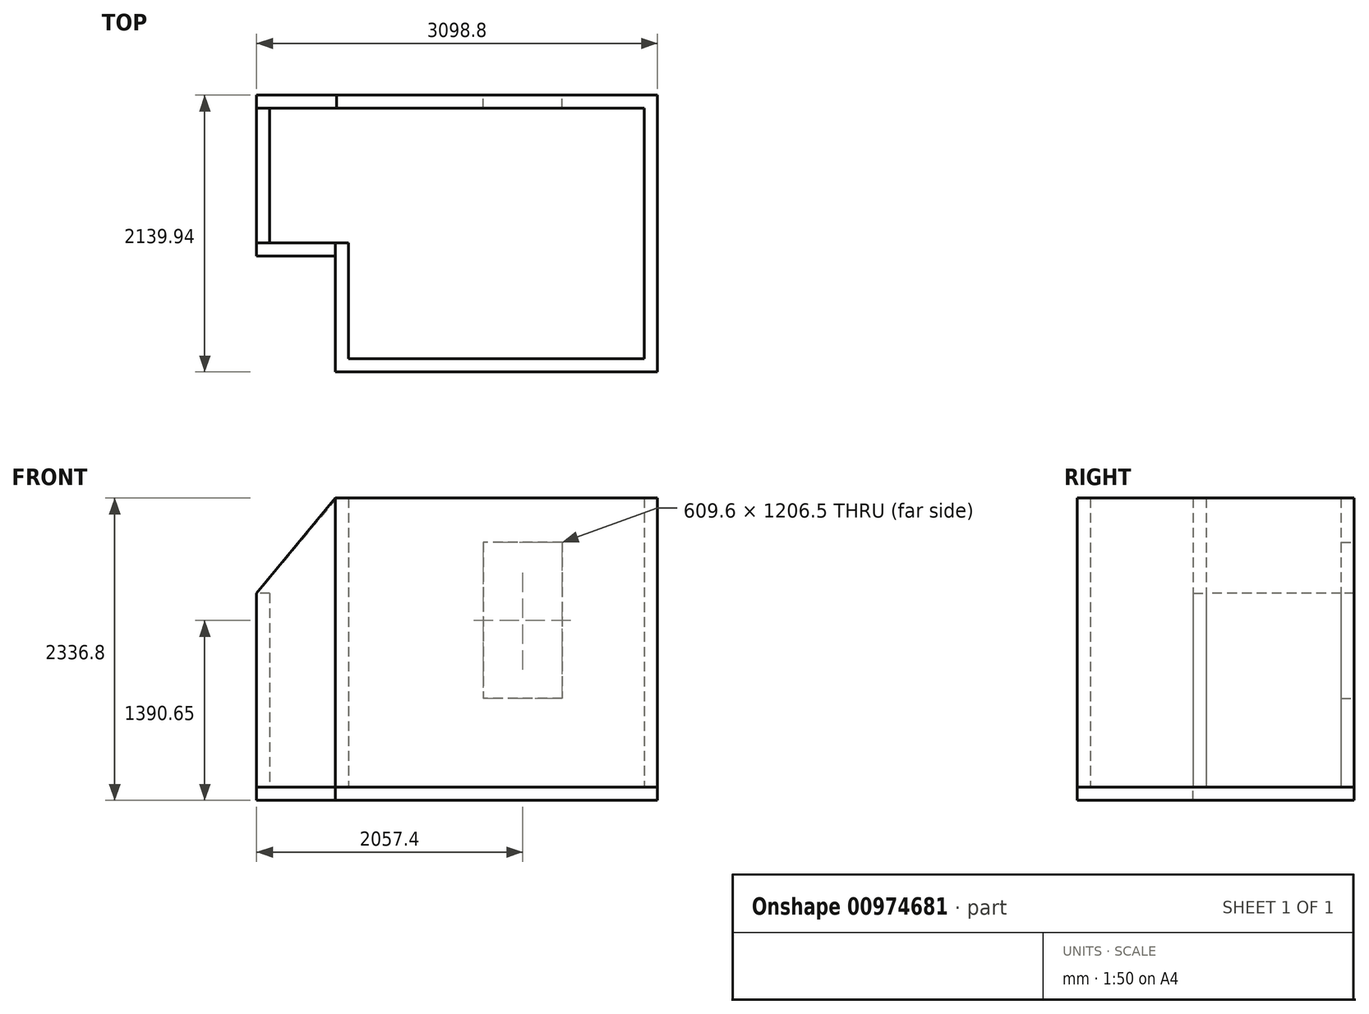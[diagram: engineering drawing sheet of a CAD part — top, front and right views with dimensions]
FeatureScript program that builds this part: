
annotation { "Feature Type Name" : "Feature", "Feature Type Description" : "" }
export const myFeature = defineFeature(function(context is Context, id is Id, definition is map)
    precondition{}
    {
        {
            var Q0;
            Q0=qCreatedBy(makeId("Top.planeOp"),FACE);
            var sketch = newSketch(context, id + "F0", { "sketchPlane" : qUnion([Q0])});
            skLineSegment(sketch, "E0.bottom", {"start": v(1143, -968.38) * mm, "end": v(-1143, -968.38) * mm});
            skLineSegment(sketch, "E0.top", {"start": v(1143, 968.38) * mm, "end": v(-1143, 968.38) * mm});
            skLineSegment(sketch, "E0.left", {"start": v(1143, -968.38) * mm, "end": v(1143, 968.38) * mm});
            skPoint(sketch, "E0.middle", {"position": v(0, 0) * mm});
            skLineSegment(sketch, "E1.bottom", {"start": v(-1143, 968.38) * mm, "end": v(-1752.6, 968.38) * mm});
            skLineSegment(sketch, "E1.top", {"start": v(-1143, -73.03) * mm, "end": v(-1752.6, -73.03) * mm});
            skLineSegment(sketch, "E1.left", {"start": v(-1143, 968.38) * mm, "end": v(-1143, -73.03) * mm});
            skLineSegment(sketch, "E1.right", {"start": v(-1752.6, 968.37) * mm, "end": v(-1752.6, -73.03) * mm});
            skPoint(sketch, "E2", {"position": v(-1143, -73.03) * mm});
            skLineSegment(sketch, "E3", {"start": v(-1143, -73.03) * mm, "end": v(-1143, -968.38) * mm});
            skLineSegment(sketch, "E4.0", {"start": v(-1244.6, -174.63) * mm, "end": v(-1244.6, -1069.98) * mm});
            skLineSegment(sketch, "E4.1", {"start": v(1244.6, -1069.97) * mm, "end": v(-1244.6, -1069.98) * mm});
            skLineSegment(sketch, "E4.2", {"start": v(-1854.2, 1069.97) * mm, "end": v(-1854.2, -174.63) * mm});
            skLineSegment(sketch, "E4.3", {"start": v(-1143, 1069.97) * mm, "end": v(-1854.2, 1069.97) * mm});
            skLineSegment(sketch, "E4.4", {"start": v(1244.6, 1069.98) * mm, "end": v(-1143, 1069.97) * mm});
            skLineSegment(sketch, "E4.5", {"start": v(-1244.6, -174.63) * mm, "end": v(-1854.2, -174.63) * mm});
            skLineSegment(sketch, "E4.6", {"start": v(1244.6, -1069.97) * mm, "end": v(1244.6, 1069.98) * mm});
            skSolve(sketch);
        }
        {
            var Q0;
            Q0=makeQuery(id+"F0.imprint","IMPRINT",FACE,{"disambiguationData":[TD([[makeQuery(id+"F0.imprint","IMPRINT",EDGE,{"derivedFrom":sQuery(id+"F0.wireOp",EDGE,"E0.bottom")}),1.0]])]});
            extrude(context, id + "F1", {"entities" : qUnion([Q0]), "depth" : 1498.6 * mm, "offsetDistance" : 25.4 * mm});
        }
        {
            var Q0;
            Q0=makeQuery(id+"F1.opExtrude","SWEPT_FACE",FACE,{"disambiguationData":[OSD([sQuery(id+"F0.wireOp",EDGE,"E4.3"),sQuery(id+"F0.wireOp",EDGE,"E4.4")])]});
            var sketch = newSketch(context, id + "F2", { "sketchPlane" : qUnion([Q0])});
            skLineSegment(sketch, "E5", {"start": v(-1244.6, 1498.6) * mm, "end": v(-1244.6, 2235.2) * mm});
            skLineSegment(sketch, "E6", {"start": v(-1244.6, 2235.2) * mm, "end": v(1236.12, 2235.2) * mm});
            skLineSegment(sketch, "E7", {"start": v(1236.12, 2235.2) * mm, "end": v(1854.2, 1498.6) * mm});
            skLineSegment(sketch, "E8", {"start": v(1854.2, 1498.6) * mm, "end": v(1854.2, 0) * mm});
            skLineSegment(sketch, "E9", {"start": v(1854.2, 0) * mm, "end": v(-1244.6, 0) * mm});
            skLineSegment(sketch, "E10", {"start": v(-1244.6, 0) * mm, "end": v(-1244.6, 1498.6) * mm});
            skLineSegment(sketch, "E11", {"start": v(1854.2, 1498.6) * mm, "end": v(-1244.6, 1498.6) * mm});
            skSolve(sketch);
        }
        {
            var Q0;
            Q0 = qSketchRegion(id + "F2", true);
            var Q1;
            Q1=makeQuery(id+"F2.imprint","IMPRINT",FACE,{"disambiguationData":[TD([[makeQuery(id+"F2.imprint","IMPRINT",EDGE,{"derivedFrom":sQuery(id+"F2.wireOp",EDGE,"E5")}),-1.0]])]});
            extrude(context, id + "F3", {"entities" : qUnion([Q0, Q1]), "operationType" : NewBodyOperationType.ADD, "oppositeDirection" : true, "depth" : 101.6 * mm, "offsetDistance" : 25.4 * mm});
        }
        {
            var Q0;
            Q0=makeQuery(id+"F1.opExtrude","CAP_FACE",FACE,{"disambiguationData":[OSD([sQuery(id+"F0.wireOp",EDGE,"E0.bottom"),sQuery(id+"F0.wireOp",EDGE,"E0.top"),sQuery(id+"F0.wireOp",EDGE,"E0.left"),sQuery(id+"F0.wireOp",EDGE,"E1.bottom"),sQuery(id+"F0.wireOp",EDGE,"E1.top"),sQuery(id+"F0.wireOp",EDGE,"E1.right"),sQuery(id+"F0.wireOp",EDGE,"E3"),sQuery(id+"F0.wireOp",EDGE,"E4.0"),sQuery(id+"F0.wireOp",EDGE,"E4.1"),sQuery(id+"F0.wireOp",EDGE,"E4.2"),sQuery(id+"F0.wireOp",EDGE,"E4.3"),sQuery(id+"F0.wireOp",EDGE,"E4.4"),sQuery(id+"F0.wireOp",EDGE,"E4.5"),sQuery(id+"F0.wireOp",EDGE,"E4.6")])],"isStart":false});
            var sketch = newSketch(context, id + "F4", { "sketchPlane" : qUnion([Q0])});
            skLineSegment(sketch, "E12", {"start": v(-1244.6, -1069.98) * mm, "end": v(-1244.6, -73.03) * mm});
            skSolve(sketch);
        }
        {
            var Q0;
            Q0 = qSketchRegion(id + "F4", true);
            var Q1;
            {var subQ1=sQuery(id+"F0.wireOp",EDGE,"E0.bottom");Q1=makeQuery(id+"F4.imprint","IMPRINT",FACE,{"disambiguationData":[TD([[makeQuery(id+"F4.imprint","IMPRINT",EDGE,{"derivedFrom":makeQuery(id+"F1.opExtrude","CAP_EDGE",EDGE,{"disambiguationData":[OSD([subQ1])],"isStart":false})}),1.0]])]});}
            var Q2;
            Q2=makeQuery(id+"F3.opExtrude","SWEPT_FACE",FACE,{"disambiguationData":[OSD([sQuery(id+"F2.wireOp",EDGE,"E6")])]});
            extrude(context, id + "F5", {"entities" : qUnion([Q0, Q1]), "operationType" : NewBodyOperationType.ADD, "endBound" : BoundingType.UP_TO_SURFACE, "depth" : 25.4 * mm, "endBoundEntityFace" : qUnion([Q2]), "offsetDistance" : 25.4 * mm});
        }
        {
            var Q0;
            {var subQ0=sQuery(id+"F0.wireOp",EDGE,"E1.top");Q0=makeQuery(id+"F5.boolean.opBoolean","MERGE",FACE,{"derivedFrom":[makeQuery(id+"F1.opExtrude","SWEPT_FACE",FACE,{"disambiguationData":[OSD([subQ0])]}),makeQuery(id+"F5.opExtrude","SWEPT_FACE",FACE,{"disambiguationData":[OSD([subQ0])]})]});}
            var sketch = newSketch(context, id + "F6", { "sketchPlane" : qUnion([Q0])});
            skLineSegment(sketch, "E13", {"start": v(1244.6, 1498.6) * mm, "end": v(1244.6, 2235.2) * mm});
            skLineSegment(sketch, "E14", {"start": v(1244.6, 2235.2) * mm, "end": v(1854.2, 1498.6) * mm});
            skLineSegment(sketch, "E15", {"start": v(1854.2, 1498.6) * mm, "end": v(1752.6, 1498.6) * mm});
            skLineSegment(sketch, "E16", {"start": v(1752.6, 1498.6) * mm, "end": v(1244.6, 1498.6) * mm});
            skSolve(sketch);
        }
        {
            var Q0;
            Q0=makeQuery(id+"F6.imprint","IMPRINT",FACE,{"disambiguationData":[TD([[makeQuery(id+"F6.imprint","IMPRINT",EDGE,{"derivedFrom":sQuery(id+"F6.wireOp",EDGE,"E13")}),1.0]])]});
            extrude(context, id + "F7", {"entities" : qUnion([Q0]), "operationType" : NewBodyOperationType.ADD, "oppositeDirection" : true, "depth" : 101.6 * mm, "offsetDistance" : 25.4 * mm});
        }
        {
            var Q0;
            Q0=makeQuery(id+"F3.boolean.opBoolean","MERGE",FACE,{"derivedFrom":[makeQuery(id+"F1.opExtrude","SWEPT_FACE",FACE,{"disambiguationData":[OSD([sQuery(id+"F0.wireOp",EDGE,"E4.3"),sQuery(id+"F0.wireOp",EDGE,"E4.4")])]}),makeQuery(id+"F3.opExtrude","CAP_FACE",FACE,{"disambiguationData":[OSD([sQuery(id+"F2.wireOp",EDGE,"E5"),sQuery(id+"F2.wireOp",EDGE,"E6"),sQuery(id+"F2.wireOp",EDGE,"E7"),sQuery(id+"F2.wireOp",EDGE,"E8"),sQuery(id+"F2.wireOp",EDGE,"E9"),sQuery(id+"F2.wireOp",EDGE,"E10")])],"isStart":true})]});
            var sketch = newSketch(context, id + "F8", { "sketchPlane" : qUnion([Q0])});
            skLineSegment(sketch, "E17.bottom", {"start": v(-508, 1892.3) * mm, "end": v(101.6, 1892.3) * mm});
            skLineSegment(sketch, "E17.top", {"start": v(-508, 685.8) * mm, "end": v(101.6, 685.8) * mm});
            skLineSegment(sketch, "E17.left", {"start": v(-508, 1892.3) * mm, "end": v(-508, 685.8) * mm});
            skLineSegment(sketch, "E17.right", {"start": v(101.6, 1892.3) * mm, "end": v(101.6, 685.8) * mm});
            skSolve(sketch);
        }
        {
            var Q0;
            Q0 = qSketchRegion(id + "F8", true);
            var Q1;
            Q1=makeQuery(id+"F8.imprint","IMPRINT",FACE,{"disambiguationData":[TD([[makeQuery(id+"F8.imprint","IMPRINT",EDGE,{"derivedFrom":sQuery(id+"F8.wireOp",EDGE,"E17.bottom")}),-1.0]])]});
            extrude(context, id + "F9", {"entities" : qUnion([Q0, Q1]), "operationType" : NewBodyOperationType.REMOVE, "oppositeDirection" : true, "depth" : 101.6 * mm, "offsetDistance" : 25.4 * mm});
        }
        {
            var Q0;
            Q0=makeQuery(id+"F0.imprint","IMPRINT",FACE,{"disambiguationData":[TD([[makeQuery(id+"F0.imprint","IMPRINT",EDGE,{"derivedFrom":sQuery(id+"F0.wireOp",EDGE,"E0.bottom")}),-1.0]])]});
            var Q1;
            Q1=makeQuery(id+"F0.imprint","IMPRINT",FACE,{"disambiguationData":[TD([[makeQuery(id+"F0.imprint","IMPRINT",EDGE,{"derivedFrom":sQuery(id+"F0.wireOp",EDGE,"E1.bottom")}),1.0]])]});
            var Q2;
            Q2=makeQuery(id+"F0.imprint","IMPRINT",FACE,{"disambiguationData":[TD([[makeQuery(id+"F0.imprint","IMPRINT",EDGE,{"derivedFrom":sQuery(id+"F0.wireOp",EDGE,"E0.bottom")}),1.0]])]});
            extrude(context, id + "F10", {"entities" : qUnion([Q0, Q1, Q2]), "oppositeDirection" : true, "depth" : 101.6 * mm, "offsetDistance" : 25.4 * mm});
        }
    });
